# Revit family: Faucet_Two_Handle-American_Standard-Colony_Soft-2475.55X_Series
name_source: partatom
category: Plumbing Fixtures
revit_build: Autodesk Revit 2018 (Build: 20170223_1515(x64)
units: mm (PartAtom-declared; Revit-internal decimal feet)

## family parameters
Always vertical = No
Cut with Voids When Loaded = No
OmniClass Number = 23.45.55.17
OmniClass Title = Mixing Faucets
Part Type = Normal
Room Calculation Point = No
Round Connector Dimension = Use Diameter
Shared = Yes
Work Plane-Based = Yes

## types (1)
- 2475550.002
    ADA Compliant = Yes
    Aerator = Yes
    Assembly Code = D2020300
    CW Connection = Yes
    CWFU = 1.5
    Cold Water Connection Diameter = 1/2"
    Compliance Certifications = These products meet or exceed the following codes and standards: ANSI A117.1. ASME A112.18.1,CSA B 125, NSF 61/Section 9
    Default Elevation = 0"
    Description = Colony® Soft 2-Handle Laundry Faucet 2.2 gpm/8.3 L/min
    Finish = Brass-American Standard-002-Polished Chrome
    Flow Rate = 2.2 gpm (8.3 L/min)
    HW Connection = Yes
    HWFU = 1.5
    Height = 4 3/4"
    Hot Water Connection Diameter = 1"
    Installation Type = Deck Mounted
    Length = 6 1/8"
    Manufacturer = American Standard
    Material = Brass-American Standard-002-Polished Chrome
    Model = 2475500.002
    Product Documentation Link = https://americanstandard.box.com
    Product Page URL = https://www.americanstandard-us.com
    Revised Date = 08/14/2022
    URL = http://www.americanstandard-us.com
    Vent Connection = No
    WFU = 2
    Warranty Information = Limited Lifetime Function and Finish Warranty
    Waste Connection = No
    Width = 2 1/8"

## geometry (parser evidence)
native form markers: Sweep x2
no freeform markers — native parametric forms only
